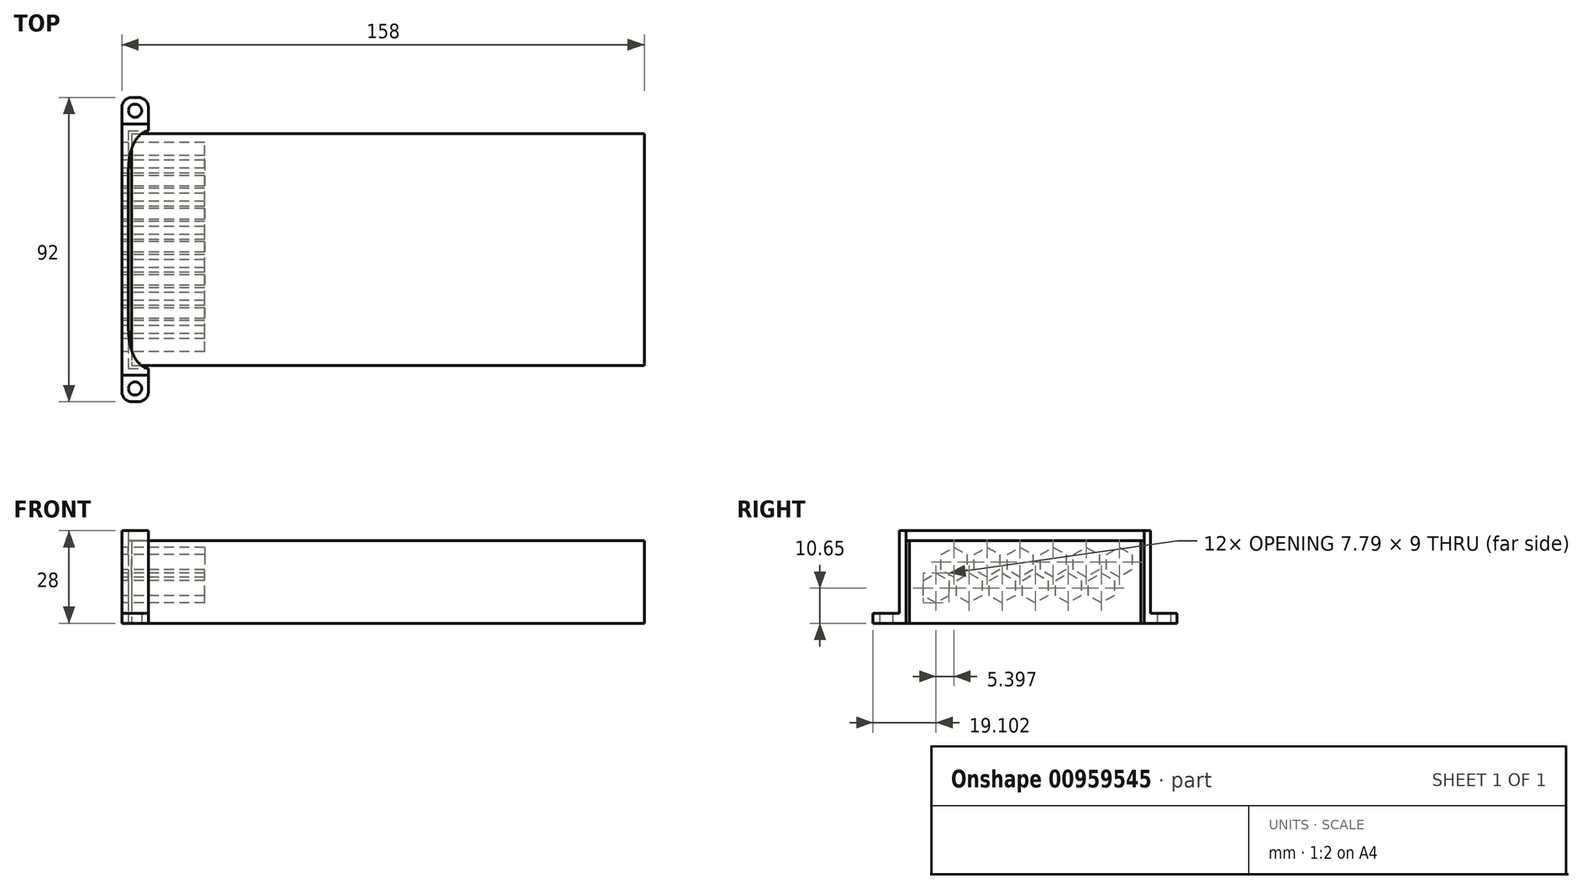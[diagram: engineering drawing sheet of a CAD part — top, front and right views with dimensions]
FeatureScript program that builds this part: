
annotation { "Feature Type Name" : "Feature", "Feature Type Description" : "" }
export const myFeature = defineFeature(function(context is Context, id is Id, definition is map)
    precondition{}
    {
        {
            var Q0;
            Q0=qCreatedBy(makeId("Top.planeOp"),FACE);
            var sketch = newSketch(context, id + "F0", { "sketchPlane" : qUnion([Q0])});
            skLineSegment(sketch, "E0.bottom", {"start": v(-69.4, 20.7) * mm, "end": v(85.6, 20.7) * mm});
            skLineSegment(sketch, "E0.top", {"start": v(-69.4, -49.3) * mm, "end": v(85.6, -49.3) * mm});
            skLineSegment(sketch, "E0.left", {"start": v(-69.4, 20.7) * mm, "end": v(-69.4, -49.3) * mm});
            skLineSegment(sketch, "E0.right", {"start": v(85.6, 20.7) * mm, "end": v(85.6, -49.3) * mm});
            skSolve(sketch);
        }
        {
            var Q0;
            Q0=makeQuery(id+"F0.imprint","IMPRINT",FACE,{"disambiguationData":[TD([[makeQuery(id+"F0.imprint","IMPRINT",EDGE,{"derivedFrom":sQuery(id+"F0.wireOp",EDGE,"E0.bottom")}),-1.0]])]});
            extrude(context, id + "F1", {"entities" : qUnion([Q0]), "depth" : 25 * mm, "offsetDistance" : 25 * mm});
        }
        {
            var Q0;
            Q0=qCreatedBy(makeId("Top.planeOp"),FACE);
            var sketch = newSketch(context, id + "F2", { "sketchPlane" : qUnion([Q0])});
            skLineSegment(sketch, "E1.0", {"start": v(-69.4, 20.7) * mm, "end": v(-69.4, -49.3) * mm});
            skLineSegment(sketch, "E2.0", {"start": v(-69.4, 20.7) * mm, "end": v(85.6, 20.7) * mm});
            skLineSegment(sketch, "E3.0", {"start": v(-69.4, -49.3) * mm, "end": v(85.6, -49.3) * mm});
            skLineSegment(sketch, "E4", {"start": v(-64.4, 20.7) * mm, "end": v(-64.4, -49.3) * mm, "construction": true});
            skLineSegment(sketch, "E5", {"start": v(-72.4, 23.7) * mm, "end": v(-72.4, -52.3) * mm});
            skLineSegment(sketch, "E6.0", {"start": v(-70.4, 21.7) * mm, "end": v(85.6, 21.7) * mm});
            skLineSegment(sketch, "E6.1", {"start": v(-70.4, 21.7) * mm, "end": v(-70.4, -50.3) * mm});
            skLineSegment(sketch, "E6.2", {"start": v(-70.4, -50.3) * mm, "end": v(85.6, -50.3) * mm});
            skPoint(sketch, "E7.endSnap0", {"position": v(-72.4, -14.3) * mm});
            skLineSegment(sketch, "E8", {"start": v(-72.4, -52.3) * mm, "end": v(-40.33, -52.3) * mm});
            skLineSegment(sketch, "E9", {"start": v(-64.4, -50.3) * mm, "end": v(-64.4, -52.3) * mm});
            skFitSpline(sketch, "E10", {"points": [v(-64.4, -50.3) * mm, v(-70.4, -38) * mm], "startDerivative": vector(-12.53, 3) * mm, "endDerivative": vector(0, 17.67) * mm});
            skCircle(sketch, "E11", {"center": v(-68.4, -56.3) * mm, "radius": 2 * mm});
            skLineSegment(sketch, "E12", {"start": v(-72.4, -52.3) * mm, "end": v(-72.4, -57.3) * mm});
            skLineSegment(sketch, "E13", {"start": v(-69.4, -60.3) * mm, "end": v(-67.4, -60.3) * mm});
            skLineSegment(sketch, "E14", {"start": v(-64.4, -57.3) * mm, "end": v(-64.4, -52.3) * mm});
            skPoint(sketch, "E15.visualSharp", {"position": v(-72.4, -60.3) * mm});
            skArc(sketch, "E15.filletArc", {"start": v(-72.4, -57.3) * mm, "mid": v(-71.52, -59.42) * mm, "end": v(-69.4, -60.3) * mm});
            skPoint(sketch, "E16.visualSharp", {"position": v(-64.4, -60.3) * mm});
            skArc(sketch, "E16.filletArc", {"start": v(-67.4, -60.3) * mm, "mid": v(-65.28, -59.42) * mm, "end": v(-64.4, -57.3) * mm});
            skLineSegment(sketch, "E17", {"start": v(-72.4, -14.3) * mm, "end": v(-70.4, -14.3) * mm});
            skLineSegment(sketch, "E18.MirrorCS", {"start": v(-69.4, 31.7) * mm, "end": v(-67.4, 31.7) * mm});
            skLineSegment(sketch, "E19.MirrorCS", {"start": v(-64.4, 21.7) * mm, "end": v(-64.4, 23.7) * mm});
            skCircle(sketch, "E20.MirrorC", {"center": v(-68.4, 27.7) * mm, "radius": 2 * mm});
            skLineSegment(sketch, "E21.MirrorCS", {"start": v(-64.4, 28.7) * mm, "end": v(-64.4, 23.7) * mm});
            skFitSpline(sketch, "E22.MirrorCS", {"points": [v(-64.4, 21.7) * mm, v(-70.4, 9.4) * mm], "startDerivative": vector(-12.53, -3) * mm, "endDerivative": vector(0, -17.67) * mm});
            skArc(sketch, "E23.MirrorCS", {"start": v(-72.4, 28.7) * mm, "mid": v(-71.52, 30.82) * mm, "end": v(-69.4, 31.7) * mm});
            skPoint(sketch, "E24.MirrorP", {"position": v(-64.4, 31.7) * mm});
            skLineSegment(sketch, "E25.MirrorCS", {"start": v(-72.4, 23.7) * mm, "end": v(-72.4, 28.7) * mm});
            skPoint(sketch, "E26.MirrorP", {"position": v(-72.4, 31.7) * mm});
            skArc(sketch, "E27.MirrorCS", {"start": v(-67.4, 31.7) * mm, "mid": v(-65.28, 30.82) * mm, "end": v(-64.4, 28.7) * mm});
            skLineSegment(sketch, "E28.MirrorCS", {"start": v(-72.4, 23.7) * mm, "end": v(-40.33, 23.7) * mm});
            skSolve(sketch);
        }
        {
            var Q0;
            {var subQ2=sQuery(id+"F2.wireOp",EDGE,"f2b4tzMf-fz64-lq1D-4F5y-ZbGM6D4Rdu9D");Q0=makeQuery(id+"F2.imprint","IMPRINT",FACE,{"disambiguationData":[TD([[makeQuery(id+"F2.imprint","IMPRINT",EDGE,{"derivedFrom":subQ2}),-1.0]])]});}
            var Q1;
            {var subQ5=sQuery(id+"F2.wireOp",EDGE,"x6Gp82Mo-5qvD-lJAC-nekq-US88aRadaIZf");Q1=makeQuery(id+"F2.imprint","IMPRINT",FACE,{"disambiguationData":[TD([[makeQuery(id+"F2.imprint","IMPRINT",EDGE,{"derivedFrom":subQ5}),1.0]])]});}
            var Q2;
            {var subQ2=sQuery(id+"F2.wireOp",EDGE,"a35ece90-018a-4ddc-90cd-08641510cc081.MirrorC");Q2=makeQuery(id+"F2.imprint","IMPRINT",FACE,{"disambiguationData":[TD([[makeQuery(id+"F2.imprint","IMPRINT",EDGE,{"derivedFrom":subQ2}),1.0]])]});}
            var Q3;
            Q3=makeQuery(id+"F2.imprint","IMPRINT",FACE,{"disambiguationData":[TD([[makeQuery(id+"F2.imprint","IMPRINT",EDGE,{"derivedFrom":sQuery(id+"F2.wireOp",EDGE,"E18.MirrorCS")}),-1.0]])]});
            var Q4;
            {var subQ0=sQuery(id+"F2.wireOp",EDGE,"E17");Q4=makeQuery(id+"F2.imprint","IMPRINT",FACE,{"disambiguationData":[TD([[makeQuery(id+"F2.imprint","IMPRINT",EDGE,{"derivedFrom":subQ0}),1.0]])]});}
            var Q5;
            {var subQ4=sQuery(id+"F2.wireOp",EDGE,"E9");Q5=makeQuery(id+"F2.imprint","IMPRINT",FACE,{"disambiguationData":[TD([[makeQuery(id+"F2.imprint","IMPRINT",EDGE,{"derivedFrom":subQ4}),-1.0]])]});}
            var Q6;
            Q6=makeQuery(id+"F2.imprint","IMPRINT",FACE,{"disambiguationData":[TD([[makeQuery(id+"F2.imprint","IMPRINT",EDGE,{"derivedFrom":sQuery(id+"F2.wireOp",EDGE,"E11")}),-1.0]])]});
            extrude(context, id + "F3", {"entities" : qUnion([Q0, Q1, Q2, Q3, Q4, Q5, Q6]), "depth" : 3 * mm, "offsetDistance" : 25 * mm});
        }
        {
            var Q0;
            {var subQ4=sQuery(id+"F2.wireOp",EDGE,"E9");Q0=makeQuery(id+"F2.imprint","IMPRINT",FACE,{"disambiguationData":[TD([[makeQuery(id+"F2.imprint","IMPRINT",EDGE,{"derivedFrom":subQ4}),-1.0]])]});}
            var Q1;
            {var subQ0=sQuery(id+"F2.wireOp",EDGE,"E17");Q1=makeQuery(id+"F2.imprint","IMPRINT",FACE,{"disambiguationData":[TD([[makeQuery(id+"F2.imprint","IMPRINT",EDGE,{"derivedFrom":subQ0}),1.0]])]});}
            var Q2;
            Q2=makeQuery(id+"F1.opExtrude","CAP_FACE",FACE,{"disambiguationData":[OSD([sQuery(id+"F0.wireOp",EDGE,"E0.bottom"),sQuery(id+"F0.wireOp",EDGE,"E0.top"),sQuery(id+"F0.wireOp",EDGE,"E0.left"),sQuery(id+"F0.wireOp",EDGE,"E0.right")])],"isStart":false});
            var Q3;
            Q3=makeQuery(id+"F1.opExtrude","SWEPT_BODY",BODY,{"disambiguationData":[OSD([sQuery(id+"F0.wireOp",EDGE,"E0.bottom"),sQuery(id+"F0.wireOp",EDGE,"E0.top"),sQuery(id+"F0.wireOp",EDGE,"E0.left"),sQuery(id+"F0.wireOp",EDGE,"E0.right")])]});
            extrude(context, id + "F4", {"entities" : qUnion([Q0, Q1]), "operationType" : NewBodyOperationType.ADD, "endBound" : BoundingType.UP_TO_SURFACE, "depth" : 25 * mm, "endBoundEntityFace" : qUnion([Q2]), "endBoundEntityBody" : qUnion([Q3]), "hasOffset" : true, "offsetDistance" : 3 * mm, "offsetOppositeDirection" : true});
        }
        {
            var Q0;
            {var subQ0=sQuery(id+"F2.wireOp",EDGE,"E2.0");var subQ1=sQuery(id+"F2.wireOp",EDGE,"E1.0");var subQ2=makeQuery(id+"F2.imprint","INTERSECT",VERTEX,{"derivedFrom":[subQ1,subQ0]});Q0=makeQuery(id+"F2.imprint","IMPRINT",FACE,{"disambiguationData":[TD([[makeQuery(id+"F2.imprint","IMPRINT",EDGE,{"disambiguationData":[TD([[subQ2,-1.0]])],"derivedFrom":subQ1}),1.0]])]});}
            var Q1;
            {var subQ6=sQuery(id+"F2.wireOp",EDGE,"E2.0");var subQ7=sQuery(id+"F2.wireOp",EDGE,"E1.0");var subQ8=makeQuery(id+"F2.imprint","INTERSECT",VERTEX,{"derivedFrom":[subQ7,subQ6]});Q1=makeQuery(id+"F2.imprint","IMPRINT",FACE,{"disambiguationData":[TD([[makeQuery(id+"F2.imprint","IMPRINT",EDGE,{"disambiguationData":[TD([[subQ8,-1.0]])],"derivedFrom":subQ7}),-1.0]])]});}
            var Q2;
            {var subQ0=sQuery(id+"F2.wireOp",EDGE,"E3.0");var subQ1=sQuery(id+"F2.wireOp",EDGE,"E1.0");var subQ2=makeQuery(id+"F2.imprint","INTERSECT",VERTEX,{"derivedFrom":[subQ1,subQ0]});Q2=makeQuery(id+"F2.imprint","IMPRINT",FACE,{"disambiguationData":[TD([[makeQuery(id+"F2.imprint","IMPRINT",EDGE,{"disambiguationData":[TD([[subQ2,1.0]])],"derivedFrom":subQ1}),1.0]])]});}
            var Q3;
            {var subQ6=sQuery(id+"F2.wireOp",EDGE,"E3.0");var subQ9=sQuery(id+"F2.wireOp",EDGE,"E1.0");var subQ10=makeQuery(id+"F2.imprint","INTERSECT",VERTEX,{"derivedFrom":[subQ9,subQ6]});Q3=makeQuery(id+"F2.imprint","IMPRINT",FACE,{"disambiguationData":[TD([[makeQuery(id+"F2.imprint","IMPRINT",EDGE,{"disambiguationData":[TD([[subQ10,1.0]])],"derivedFrom":subQ9}),-1.0]])]});}
            var Q4;
            Q4=makeQuery(id+"F1.opExtrude","CAP_FACE",FACE,{"disambiguationData":[OSD([sQuery(id+"F0.wireOp",EDGE,"E0.bottom"),sQuery(id+"F0.wireOp",EDGE,"E0.top"),sQuery(id+"F0.wireOp",EDGE,"E0.left"),sQuery(id+"F0.wireOp",EDGE,"E0.right")])],"isStart":false});
            extrude(context, id + "F5", {"entities" : qUnion([Q0, Q1, Q2, Q3]), "operationType" : NewBodyOperationType.ADD, "depth" : 28 * mm, "endBoundEntityFace" : qUnion([Q4]), "offsetDistance" : 25 * mm, "hasSecondDirection" : true, "secondDirectionOppositeDirection" : false, "secondDirectionDepth" : 25 * mm});
        }
        {
            var Q0;
            {var subQ0=sQuery(id+"F2.wireOp",EDGE,"E5");Q0=makeQuery(id+"F4.boolean.opBoolean","MERGE",FACE,{"derivedFrom":[makeQuery(id+"F3.opExtrude","SWEPT_FACE",FACE,{"disambiguationData":[OSD([subQ0,sQuery(id+"F2.wireOp",EDGE,"E12"),sQuery(id+"F2.wireOp",EDGE,"E25.MirrorCS")])]}),makeQuery(id+"F4.opExtrude","SWEPT_FACE",FACE,{"disambiguationData":[OSD([subQ0])]})]});}
            var sketch = newSketch(context, id + "F6", { "sketchPlane" : qUnion([Q0])});
            skLineSegment(sketch, "E29.0", {"start": v(-23.7, 28) * mm, "end": v(-23.7, 3) * mm});
            skLineSegment(sketch, "E30.0", {"start": v(-23.7, 28) * mm, "end": v(52.3, 28) * mm});
            skLineSegment(sketch, "E31.0", {"start": v(52.3, 28) * mm, "end": v(52.3, 3) * mm});
            skLineSegment(sketch, "E32.0", {"start": v(52.3, 0) * mm, "end": v(-23.7, 0) * mm});
            skLineSegment(sketch, "E33", {"start": v(-23.7, 3) * mm, "end": v(-23.7, 0) * mm});
            skLineSegment(sketch, "E34", {"start": v(52.3, 3) * mm, "end": v(52.3, 0) * mm});
            skPoint(sketch, "E35.orphan", {"position": v(57.3, 0) * mm});
            skPoint(sketch, "E36.orphan", {"position": v(-28.7, 0) * mm});
            skLineSegment(sketch, "E37.0", {"start": v(-18.7, 23) * mm, "end": v(-18.7, 5) * mm, "construction": true});
            skLineSegment(sketch, "E37.1", {"start": v(-18.7, 23) * mm, "end": v(47.3, 23) * mm, "construction": true});
            skLineSegment(sketch, "E37.2", {"start": v(47.3, 23) * mm, "end": v(47.3, 5) * mm, "construction": true});
            skLineSegment(sketch, "E37.3", {"start": v(47.3, 5) * mm, "end": v(-18.7, 5) * mm, "construction": true});
            skLineSegment(sketch, "E38", {"start": v(-18.7, 14) * mm, "end": v(47.3, 14) * mm, "construction": true});
            skLineSegment(sketch, "E39", {"start": v(-9.7, 23) * mm, "end": v(-9.7, 14) * mm, "construction": true});
            skLineSegment(sketch, "E40", {"start": v(-9.7, 18.5) * mm, "end": v(-18.7, 18.5) * mm, "construction": true});
            skCircle(sketch, "E41.cCircle", {"center": v(-14.2, 18.5) * mm, "radius": 4.5 * mm, "construction": true});
            skPoint(sketch, "E41.cCircle.perimeterSnap0", {"position": v(-14.2, 18.5) * mm});
            skLineSegment(sketch, "E41.0", {"start": v(-14.2, 14) * mm, "end": v(-18.1, 16.25) * mm});
            skPoint(sketch, "E41.0.startSnap0", {"position": v(-14.2, 18.5) * mm});
            skLineSegment(sketch, "E41.1", {"start": v(-18.1, 16.25) * mm, "end": v(-18.1, 20.75) * mm});
            skLineSegment(sketch, "E41.2", {"start": v(-18.1, 20.75) * mm, "end": v(-14.2, 23) * mm});
            skLineSegment(sketch, "E41.3", {"start": v(-14.2, 23) * mm, "end": v(-10.3, 20.75) * mm});
            skLineSegment(sketch, "E41.4", {"start": v(-10.3, 20.75) * mm, "end": v(-10.3, 16.25) * mm});
            skLineSegment(sketch, "E41.5", {"start": v(-10.3, 16.25) * mm, "end": v(-14.2, 14) * mm});
            skLineSegment(sketch, "E42.1.0.0", {"start": v(-8.1, 20.75) * mm, "end": v(-4.2, 23) * mm});
            skLineSegment(sketch, "E42.1.0.1", {"start": v(-4.2, 23) * mm, "end": v(-0.3, 20.75) * mm});
            skLineSegment(sketch, "E42.1.0.2", {"start": v(-0.3, 20.75) * mm, "end": v(-0.3, 16.25) * mm});
            skLineSegment(sketch, "E42.1.0.3", {"start": v(-0.3, 16.25) * mm, "end": v(-4.2, 14) * mm});
            skLineSegment(sketch, "E42.1.0.4", {"start": v(-4.2, 14) * mm, "end": v(-8.1, 16.25) * mm});
            skLineSegment(sketch, "E42.1.0.5", {"start": v(-8.1, 16.25) * mm, "end": v(-8.1, 20.75) * mm});
            skLineSegment(sketch, "E42.2.0.0", {"start": v(1.9, 20.75) * mm, "end": v(5.8, 23) * mm});
            skLineSegment(sketch, "E42.2.0.1", {"start": v(5.8, 23) * mm, "end": v(9.7, 20.75) * mm});
            skLineSegment(sketch, "E42.2.0.2", {"start": v(9.7, 20.75) * mm, "end": v(9.7, 16.25) * mm});
            skLineSegment(sketch, "E42.2.0.3", {"start": v(9.7, 16.25) * mm, "end": v(5.8, 14) * mm});
            skLineSegment(sketch, "E42.2.0.4", {"start": v(5.8, 14) * mm, "end": v(1.9, 16.25) * mm});
            skLineSegment(sketch, "E42.2.0.5", {"start": v(1.9, 16.25) * mm, "end": v(1.9, 20.75) * mm});
            skLineSegment(sketch, "E42.3.0.0", {"start": v(11.9, 20.75) * mm, "end": v(15.8, 23) * mm});
            skLineSegment(sketch, "E42.3.0.1", {"start": v(15.8, 23) * mm, "end": v(19.7, 20.75) * mm});
            skLineSegment(sketch, "E42.3.0.2", {"start": v(19.7, 20.75) * mm, "end": v(19.7, 16.25) * mm});
            skLineSegment(sketch, "E42.3.0.3", {"start": v(19.7, 16.25) * mm, "end": v(15.8, 14) * mm});
            skLineSegment(sketch, "E42.3.0.4", {"start": v(15.8, 14) * mm, "end": v(11.9, 16.25) * mm});
            skLineSegment(sketch, "E42.3.0.5", {"start": v(11.9, 16.25) * mm, "end": v(11.9, 20.75) * mm});
            skLineSegment(sketch, "E42.4.0.0", {"start": v(21.9, 20.75) * mm, "end": v(25.8, 23) * mm});
            skLineSegment(sketch, "E42.4.0.1", {"start": v(25.8, 23) * mm, "end": v(29.7, 20.75) * mm});
            skLineSegment(sketch, "E42.4.0.2", {"start": v(29.7, 20.75) * mm, "end": v(29.7, 16.25) * mm});
            skLineSegment(sketch, "E42.4.0.3", {"start": v(29.7, 16.25) * mm, "end": v(25.8, 14) * mm});
            skLineSegment(sketch, "E42.4.0.4", {"start": v(25.8, 14) * mm, "end": v(21.9, 16.25) * mm});
            skLineSegment(sketch, "E42.4.0.5", {"start": v(21.9, 16.25) * mm, "end": v(21.9, 20.75) * mm});
            skLineSegment(sketch, "E42.5.0.0", {"start": v(31.9, 20.75) * mm, "end": v(35.8, 23) * mm});
            skLineSegment(sketch, "E42.5.0.1", {"start": v(35.8, 23) * mm, "end": v(39.7, 20.75) * mm});
            skLineSegment(sketch, "E42.5.0.2", {"start": v(39.7, 20.75) * mm, "end": v(39.7, 16.25) * mm});
            skLineSegment(sketch, "E42.5.0.3", {"start": v(39.7, 16.25) * mm, "end": v(35.8, 14) * mm});
            skLineSegment(sketch, "E42.5.0.4", {"start": v(35.8, 14) * mm, "end": v(31.9, 16.25) * mm});
            skLineSegment(sketch, "E42.5.0.5", {"start": v(31.9, 16.25) * mm, "end": v(31.9, 20.75) * mm});
            skLineSegment(sketch, "E42.direction1", {"start": v(-18.1, 20.75) * mm, "end": v(-8.1, 20.75) * mm, "construction": true});
            skLineSegment(sketch, "E43.1.0.0", {"start": v(-12.7, 12.9) * mm, "end": v(-8.8, 15.15) * mm});
            skLineSegment(sketch, "E43.1.0.1", {"start": v(-8.8, 15.15) * mm, "end": v(-4.9, 12.9) * mm});
            skLineSegment(sketch, "E43.1.0.2", {"start": v(-4.9, 12.9) * mm, "end": v(-4.9, 8.4) * mm});
            skLineSegment(sketch, "E43.1.0.3", {"start": v(-4.9, 8.4) * mm, "end": v(-8.8, 6.15) * mm});
            skLineSegment(sketch, "E43.1.0.4", {"start": v(-8.8, 6.15) * mm, "end": v(-12.7, 8.4) * mm});
            skLineSegment(sketch, "E43.1.0.5", {"start": v(-12.7, 8.4) * mm, "end": v(-12.7, 12.9) * mm});
            skLineSegment(sketch, "E44.1.0.0", {"start": v(1.2, 6.15) * mm, "end": v(-2.7, 8.4) * mm});
            skLineSegment(sketch, "E44.1.0.1", {"start": v(-2.7, 8.4) * mm, "end": v(-2.7, 12.9) * mm});
            skLineSegment(sketch, "E44.1.0.2", {"start": v(-2.7, 12.9) * mm, "end": v(1.2, 15.15) * mm});
            skLineSegment(sketch, "E44.1.0.3", {"start": v(1.2, 15.15) * mm, "end": v(5.1, 12.9) * mm});
            skLineSegment(sketch, "E44.1.0.4", {"start": v(5.1, 12.9) * mm, "end": v(5.1, 8.4) * mm});
            skLineSegment(sketch, "E44.1.0.5", {"start": v(5.1, 8.4) * mm, "end": v(1.2, 6.15) * mm});
            skLineSegment(sketch, "E44.2.0.0", {"start": v(11.2, 6.15) * mm, "end": v(7.3, 8.4) * mm});
            skLineSegment(sketch, "E44.2.0.1", {"start": v(7.3, 8.4) * mm, "end": v(7.3, 12.9) * mm});
            skLineSegment(sketch, "E44.2.0.2", {"start": v(7.3, 12.9) * mm, "end": v(11.2, 15.15) * mm});
            skLineSegment(sketch, "E44.2.0.3", {"start": v(11.2, 15.15) * mm, "end": v(15.1, 12.9) * mm});
            skLineSegment(sketch, "E44.2.0.4", {"start": v(15.1, 12.9) * mm, "end": v(15.1, 8.4) * mm});
            skLineSegment(sketch, "E44.2.0.5", {"start": v(15.1, 8.4) * mm, "end": v(11.2, 6.15) * mm});
            skLineSegment(sketch, "E44.3.0.0", {"start": v(21.2, 6.15) * mm, "end": v(17.3, 8.4) * mm});
            skLineSegment(sketch, "E44.3.0.1", {"start": v(17.3, 8.4) * mm, "end": v(17.3, 12.9) * mm});
            skLineSegment(sketch, "E44.3.0.2", {"start": v(17.3, 12.9) * mm, "end": v(21.2, 15.15) * mm});
            skLineSegment(sketch, "E44.3.0.3", {"start": v(21.2, 15.15) * mm, "end": v(25.1, 12.9) * mm});
            skLineSegment(sketch, "E44.3.0.4", {"start": v(25.1, 12.9) * mm, "end": v(25.1, 8.4) * mm});
            skLineSegment(sketch, "E44.3.0.5", {"start": v(25.1, 8.4) * mm, "end": v(21.2, 6.15) * mm});
            skLineSegment(sketch, "E44.4.0.0", {"start": v(31.2, 6.15) * mm, "end": v(27.3, 8.4) * mm});
            skLineSegment(sketch, "E44.4.0.1", {"start": v(27.3, 8.4) * mm, "end": v(27.3, 12.9) * mm});
            skLineSegment(sketch, "E44.4.0.2", {"start": v(27.3, 12.9) * mm, "end": v(31.2, 15.15) * mm});
            skLineSegment(sketch, "E44.4.0.3", {"start": v(31.2, 15.15) * mm, "end": v(35.1, 12.9) * mm});
            skLineSegment(sketch, "E44.4.0.4", {"start": v(35.1, 12.9) * mm, "end": v(35.1, 8.4) * mm});
            skLineSegment(sketch, "E44.4.0.5", {"start": v(35.1, 8.4) * mm, "end": v(31.2, 6.15) * mm});
            skLineSegment(sketch, "E44.5.0.0", {"start": v(41.2, 6.15) * mm, "end": v(37.3, 8.4) * mm});
            skLineSegment(sketch, "E44.5.0.1", {"start": v(37.3, 8.4) * mm, "end": v(37.3, 12.9) * mm});
            skLineSegment(sketch, "E44.5.0.2", {"start": v(37.3, 12.9) * mm, "end": v(41.2, 15.15) * mm});
            skLineSegment(sketch, "E44.5.0.3", {"start": v(41.2, 15.15) * mm, "end": v(45.1, 12.9) * mm});
            skLineSegment(sketch, "E44.5.0.4", {"start": v(45.1, 12.9) * mm, "end": v(45.1, 8.4) * mm});
            skLineSegment(sketch, "E44.5.0.5", {"start": v(45.1, 8.4) * mm, "end": v(41.2, 6.15) * mm});
            skLineSegment(sketch, "E44.direction1", {"start": v(-12.7, 8.4) * mm, "end": v(-2.7, 8.4) * mm, "construction": true});
            skSolve(sketch);
        }
        {
            var Q0;
            Q0=makeQuery(id+"F6.imprint","IMPRINT",FACE,{"disambiguationData":[TD([[makeQuery(id+"F6.imprint","IMPRINT",EDGE,{"derivedFrom":sQuery(id+"F6.wireOp",EDGE,"E41.0")}),-1.0]])]});
            var Q1;
            Q1=makeQuery(id+"F6.imprint","IMPRINT",FACE,{"disambiguationData":[TD([[makeQuery(id+"F6.imprint","IMPRINT",EDGE,{"derivedFrom":sQuery(id+"F6.wireOp",EDGE,"E42.1.0.0")}),-1.0]])]});
            var Q2;
            Q2=makeQuery(id+"F6.imprint","IMPRINT",FACE,{"disambiguationData":[TD([[makeQuery(id+"F6.imprint","IMPRINT",EDGE,{"derivedFrom":sQuery(id+"F6.wireOp",EDGE,"E42.2.0.0")}),-1.0]])]});
            var Q3;
            Q3=makeQuery(id+"F6.imprint","IMPRINT",FACE,{"disambiguationData":[TD([[makeQuery(id+"F6.imprint","IMPRINT",EDGE,{"derivedFrom":sQuery(id+"F6.wireOp",EDGE,"E42.3.0.0")}),-1.0]])]});
            var Q4;
            Q4=makeQuery(id+"F6.imprint","IMPRINT",FACE,{"disambiguationData":[TD([[makeQuery(id+"F6.imprint","IMPRINT",EDGE,{"derivedFrom":sQuery(id+"F6.wireOp",EDGE,"E42.4.0.0")}),-1.0]])]});
            var Q5;
            Q5=makeQuery(id+"F6.imprint","IMPRINT",FACE,{"disambiguationData":[TD([[makeQuery(id+"F6.imprint","IMPRINT",EDGE,{"derivedFrom":sQuery(id+"F6.wireOp",EDGE,"E42.5.0.0")}),-1.0]])]});
            var Q6;
            Q6=makeQuery(id+"F6.imprint","IMPRINT",FACE,{"disambiguationData":[TD([[makeQuery(id+"F6.imprint","IMPRINT",EDGE,{"derivedFrom":sQuery(id+"F6.wireOp",EDGE,"E44.5.0.0")}),-1.0]])]});
            var Q7;
            Q7=makeQuery(id+"F6.imprint","IMPRINT",FACE,{"disambiguationData":[TD([[makeQuery(id+"F6.imprint","IMPRINT",EDGE,{"derivedFrom":sQuery(id+"F6.wireOp",EDGE,"E44.4.0.0")}),-1.0]])]});
            var Q8;
            Q8=makeQuery(id+"F6.imprint","IMPRINT",FACE,{"disambiguationData":[TD([[makeQuery(id+"F6.imprint","IMPRINT",EDGE,{"derivedFrom":sQuery(id+"F6.wireOp",EDGE,"E44.3.0.0")}),-1.0]])]});
            var Q9;
            Q9=makeQuery(id+"F6.imprint","IMPRINT",FACE,{"disambiguationData":[TD([[makeQuery(id+"F6.imprint","IMPRINT",EDGE,{"derivedFrom":sQuery(id+"F6.wireOp",EDGE,"E44.2.0.0")}),-1.0]])]});
            var Q10;
            Q10=makeQuery(id+"F6.imprint","IMPRINT",FACE,{"disambiguationData":[TD([[makeQuery(id+"F6.imprint","IMPRINT",EDGE,{"derivedFrom":sQuery(id+"F6.wireOp",EDGE,"E44.1.0.0")}),-1.0]])]});
            var Q11;
            Q11=makeQuery(id+"F6.imprint","IMPRINT",FACE,{"disambiguationData":[TD([[makeQuery(id+"F6.imprint","IMPRINT",EDGE,{"derivedFrom":sQuery(id+"F6.wireOp",EDGE,"E43.1.0.0")}),-1.0]])]});
            extrude(context, id + "F7", {"entities" : qUnion([Q0, Q1, Q2, Q3, Q4, Q5, Q6, Q7, Q8, Q9, Q10, Q11]), "operationType" : NewBodyOperationType.REMOVE, "oppositeDirection" : true, "depth" : 25 * mm, "offsetDistance" : 25 * mm});
        }
    });
